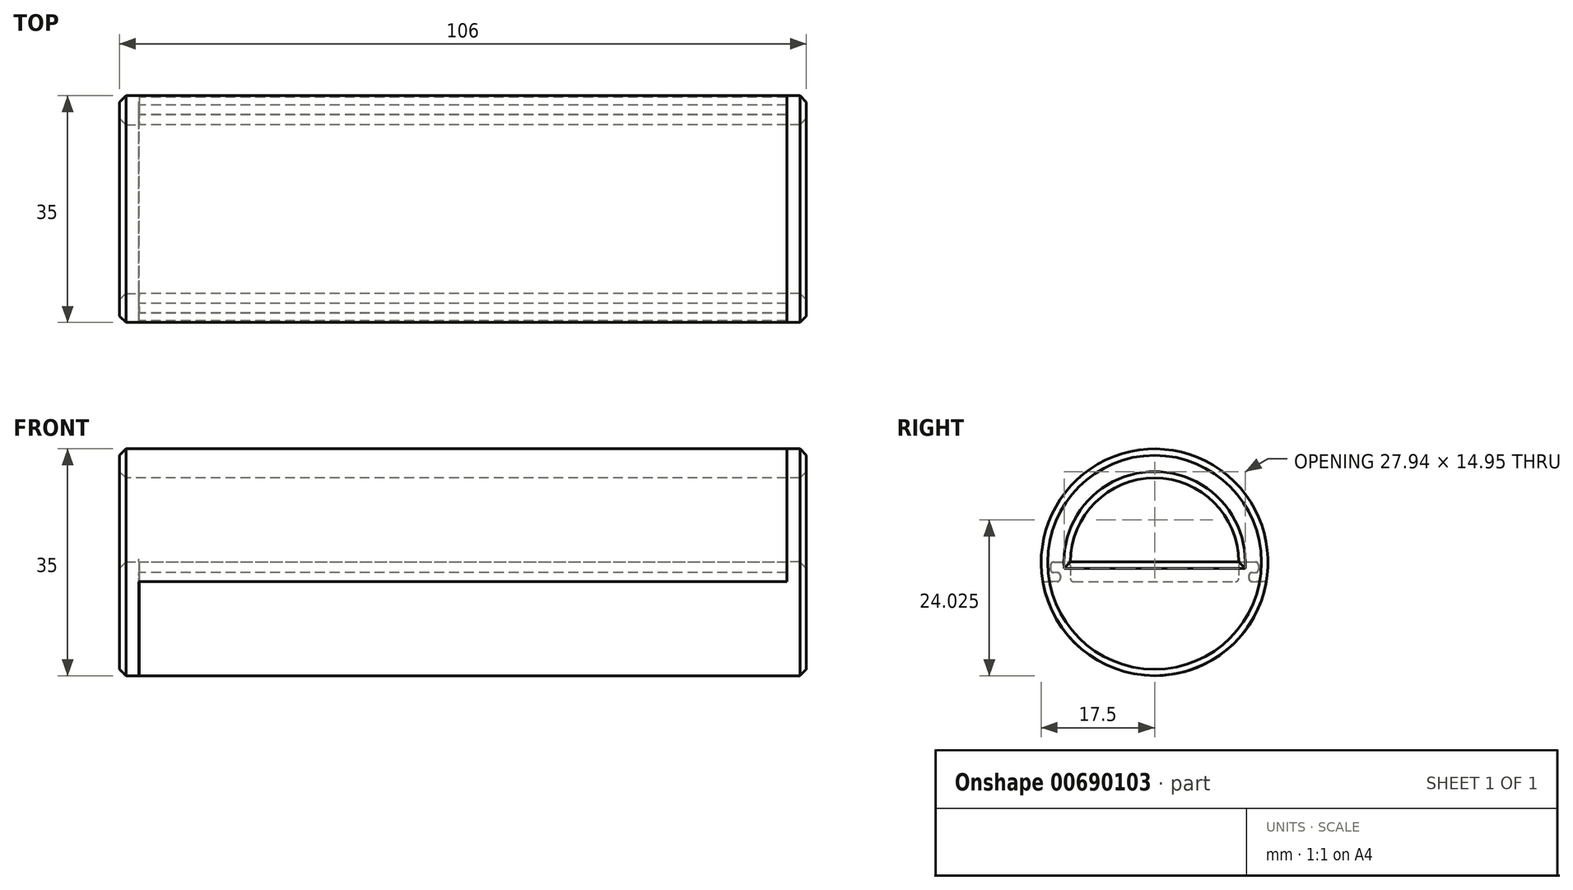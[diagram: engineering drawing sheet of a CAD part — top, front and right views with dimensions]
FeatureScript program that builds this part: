
annotation { "Feature Type Name" : "Feature", "Feature Type Description" : "" }
export const myFeature = defineFeature(function(context is Context, id is Id, definition is map)
    precondition{}
    {
        {
            var Q0;
            Q0=qCreatedBy(makeId("Right.planeOp"),FACE);
            var sketch = newSketch(context, id + "F0", { "sketchPlane" : qUnion([Q0])});
            skCircle(sketch, "E0", {"center": v(0, 0) * mm, "radius": 17.5 * mm});
            skLineSegment(sketch, "E1.top", {"start": v(-17.24, -3) * mm, "end": v(-14.53, -3) * mm});
            skLineSegment(sketch, "E1.right", {"start": v(-14.53, -1.56) * mm, "end": v(-14.53, -3) * mm});
            skLineSegment(sketch, "E2.top", {"start": v(-14.53, -1.56) * mm, "end": v(-16.03, -1.56) * mm});
            skLineSegment(sketch, "E2.right", {"start": v(-16.03, 0) * mm, "end": v(-16.03, -1.56) * mm});
            skLineSegment(sketch, "E3", {"start": v(-13, 0) * mm, "end": v(-13, -3) * mm});
            skPoint(sketch, "E4.orphan", {"position": v(-17.5, 0) * mm});
            skLineSegment(sketch, "E5", {"start": v(-16.03, 0) * mm, "end": v(-13, 0) * mm});
            skLineSegment(sketch, "E6.3", {"start": v(-14.58, -1.6) * mm, "end": v(-14.58, -2.95) * mm});
            skLineSegment(sketch, "E6.4", {"start": v(-14.58, -1.6) * mm, "end": v(-16.08, -1.6) * mm});
            skLineSegment(sketch, "E6.5", {"start": v(-16.08, 0.05) * mm, "end": v(-16.08, -1.6) * mm});
            skLineSegment(sketch, "E7", {"start": v(-14.58, -2.95) * mm, "end": v(-17.25, -2.95) * mm});
            skLineSegment(sketch, "E8.MirrorCS", {"start": v(14.58, -2.95) * mm, "end": v(17.25, -2.95) * mm});
            skLineSegment(sketch, "E9.MirrorCS", {"start": v(16.03, 0) * mm, "end": v(16.03, -1.56) * mm});
            skLineSegment(sketch, "E10.MirrorCS", {"start": v(14.53, -1.56) * mm, "end": v(16.03, -1.56) * mm});
            skLineSegment(sketch, "E11.MirrorCS", {"start": v(16.03, 0) * mm, "end": v(13, 0) * mm});
            skLineSegment(sketch, "E12.MirrorCS", {"start": v(14.53, -1.56) * mm, "end": v(14.53, -3) * mm});
            skLineSegment(sketch, "E13.MirrorCS", {"start": v(14.58, -1.6) * mm, "end": v(14.58, -2.95) * mm});
            skLineSegment(sketch, "E14.MirrorCS", {"start": v(16.08, 0.05) * mm, "end": v(16.08, -1.6) * mm});
            skLineSegment(sketch, "E15.MirrorCS", {"start": v(17.24, -3) * mm, "end": v(14.53, -3) * mm});
            skLineSegment(sketch, "E16.MirrorCS", {"start": v(13, 0) * mm, "end": v(13, -3) * mm});
            skPoint(sketch, "E17.MirrorP", {"position": v(17.5, 0) * mm});
            skLineSegment(sketch, "E18.MirrorCS", {"start": v(14.58, -1.6) * mm, "end": v(16.08, -1.6) * mm});
            skLineSegment(sketch, "E19", {"start": v(-13, -3) * mm, "end": v(13, -3) * mm});
            skLineSegment(sketch, "E20", {"start": v(-16.08, 0.05) * mm, "end": v(16.08, 0.05) * mm});
            skArc(sketch, "E21", {"start": v(13, 0) * mm, "mid": v(0, 13) * mm, "end": v(-13, 0) * mm});
            skSolve(sketch);
        }
        {
            var Q0;
            Q0=makeQuery(id+"F0.imprint","IMPRINT",FACE,{"disambiguationData":[TD([[makeQuery(id+"F0.imprint","IMPRINT",EDGE,{"derivedFrom":sQuery(id+"F0.wireOp",EDGE,"E6.3")}),-1.0]])]});
            extrude(context, id + "F1", {"entities" : qUnion([Q0]), "depth" : 99.97 * mm, "offsetDistance" : 25 * mm});
        }
        {
            var Q0;
            Q0 = qSketchRegion(id + "F0", true);
            var Q1;
            {var subQ0=sQuery(id+"F0.wireOp",EDGE,"E21");var subQ1=sQuery(id+"F0.wireOp",EDGE,"E20");var subQ2=makeQuery(id+"F0.imprint","INTERSECT",VERTEX,{"disambiguationData":[OD(0.0)],"derivedFrom":[subQ1,subQ0]});Q1=makeQuery(id+"F0.imprint","IMPRINT",FACE,{"disambiguationData":[TD([[makeQuery(id+"F0.imprint","IMPRINT",EDGE,{"disambiguationData":[TD([[subQ2,-1.0]])],"derivedFrom":subQ1}),1.0]])]});}
            var Q2;
            {var subQ5=sQuery(id+"F0.wireOp",EDGE,"E3");Q2=makeQuery(id+"F0.imprint","IMPRINT",FACE,{"disambiguationData":[TD([[makeQuery(id+"F0.imprint","IMPRINT",EDGE,{"derivedFrom":subQ5}),1.0]])]});}
            extrude(context, id + "F2", {"entities" : qUnion([Q0, Q1, Q2]), "operationType" : NewBodyOperationType.ADD, "oppositeDirection" : true, "depth" : 3 * mm, "offsetDistance" : 25 * mm});
        }
        {
            var Q0;
            {var subQ0=sQuery(id+"F0.wireOp",EDGE,"E1.top");Q0=makeQuery(id+"F0.imprint","IMPRINT",FACE,{"disambiguationData":[TD([[makeQuery(id+"F0.imprint","IMPRINT",EDGE,{"derivedFrom":subQ0}),-1.0]])]});}
            extrude(context, id + "F3", {"entities" : qUnion([Q0]), "depth" : 100 * mm, "offsetDistance" : 25 * mm, "hasSecondDirection" : true, "secondDirectionOppositeDirection" : false, "secondDirectionDepth" : 0.03 * mm});
        }
        {
            var Q0;
            Q0 = qSketchRegion(id + "F0", true);
            var Q1;
            {var subQ0=sQuery(id+"F0.wireOp",EDGE,"E21");var subQ1=sQuery(id+"F0.wireOp",EDGE,"E20");var subQ2=makeQuery(id+"F0.imprint","INTERSECT",VERTEX,{"disambiguationData":[OD(0.0)],"derivedFrom":[subQ1,subQ0]});Q1=makeQuery(id+"F0.imprint","IMPRINT",FACE,{"disambiguationData":[TD([[makeQuery(id+"F0.imprint","IMPRINT",EDGE,{"disambiguationData":[TD([[subQ2,-1.0]])],"derivedFrom":subQ1}),1.0]])]});}
            var Q2;
            {var subQ5=sQuery(id+"F0.wireOp",EDGE,"E3");Q2=makeQuery(id+"F0.imprint","IMPRINT",FACE,{"disambiguationData":[TD([[makeQuery(id+"F0.imprint","IMPRINT",EDGE,{"derivedFrom":subQ5}),1.0]])]});}
            extrude(context, id + "F4", {"entities" : qUnion([Q0, Q1, Q2]), "operationType" : NewBodyOperationType.ADD, "depth" : 103 * mm, "offsetDistance" : 25 * mm, "hasSecondDirection" : true, "secondDirectionOppositeDirection" : false, "secondDirectionDepth" : 100 * mm});
        }
        {
            var Q0;
            Q0=makeQuery(id+"F2.opExtrude","CAP_FACE",FACE,{"disambiguationData":[OSD([sQuery(id+"F0.wireOp",EDGE,"E0")])],"isStart":false});
            var Q1;
            Q1=makeQuery(id+"F4.opExtrude","CAP_FACE",FACE,{"disambiguationData":[OSD([sQuery(id+"F0.wireOp",EDGE,"E0")])],"isStart":false});
            chamfer(context, id + "F5", {"entities" : qUnion([Q0, Q1]), "width" : 1 * mm, "tangentPropagation" : true});
        }
        {
            var Q0;
            Q0=makeQuery(id+"F3.opExtrude","SWEPT_EDGE",EDGE,{"disambiguationData":[OSD([sQuery(id+"F0.wireOp",EDGE,"E11.MirrorCS"),sQuery(id+"F0.wireOp",EDGE,"E16.MirrorCS")])]});
            var Q1;
            Q1=makeQuery(id+"F1.opExtrude","SWEPT_EDGE",EDGE,{"disambiguationData":[OSD([sQuery(id+"F0.wireOp",EDGE,"E14.MirrorCS"),sQuery(id+"F0.wireOp",EDGE,"E20")])]});
            var Q2;
            Q2=makeQuery(id+"F3.opExtrude","SWEPT_EDGE",EDGE,{"disambiguationData":[OSD([sQuery(id+"F0.wireOp",EDGE,"E9.MirrorCS"),sQuery(id+"F0.wireOp",EDGE,"E11.MirrorCS")])]});
            var Q3;
            Q3=makeQuery(id+"F1.opExtrude","SWEPT_EDGE",EDGE,{"disambiguationData":[OSD([sQuery(id+"F0.wireOp",EDGE,"E14.MirrorCS"),sQuery(id+"F0.wireOp",EDGE,"E18.MirrorCS")])]});
            var Q4;
            Q4=makeQuery(id+"F3.opExtrude","SWEPT_EDGE",EDGE,{"disambiguationData":[OSD([sQuery(id+"F0.wireOp",EDGE,"E9.MirrorCS"),sQuery(id+"F0.wireOp",EDGE,"E10.MirrorCS")])]});
            var Q5;
            Q5=makeQuery(id+"F3.opExtrude","SWEPT_EDGE",EDGE,{"disambiguationData":[OSD([sQuery(id+"F0.wireOp",EDGE,"E10.MirrorCS"),sQuery(id+"F0.wireOp",EDGE,"E12.MirrorCS")])]});
            var Q6;
            Q6=makeQuery(id+"F1.opExtrude","SWEPT_EDGE",EDGE,{"disambiguationData":[OSD([sQuery(id+"F0.wireOp",EDGE,"E13.MirrorCS"),sQuery(id+"F0.wireOp",EDGE,"E18.MirrorCS")])]});
            var Q7;
            Q7=makeQuery(id+"F3.opExtrude","SWEPT_EDGE",EDGE,{"disambiguationData":[OSD([sQuery(id+"F0.wireOp",EDGE,"E16.MirrorCS"),sQuery(id+"F0.wireOp",EDGE,"E19")])]});
            var Q8;
            Q8=makeQuery(id+"F1.opExtrude","SWEPT_EDGE",EDGE,{"disambiguationData":[OSD([sQuery(id+"F0.wireOp",EDGE,"E8.MirrorCS"),sQuery(id+"F0.wireOp",EDGE,"E13.MirrorCS")])]});
            var Q9;
            Q9=makeQuery(id+"F3.opExtrude","SWEPT_EDGE",EDGE,{"disambiguationData":[OSD([sQuery(id+"F0.wireOp",EDGE,"E12.MirrorCS"),sQuery(id+"F0.wireOp",EDGE,"E15.MirrorCS")])]});
            var Q10;
            Q10=makeQuery(id+"F3.opExtrude","SWEPT_EDGE",EDGE,{"disambiguationData":[OSD([sQuery(id+"F0.wireOp",EDGE,"E3"),sQuery(id+"F0.wireOp",EDGE,"E5")])]});
            var Q11;
            Q11=makeQuery(id+"F3.opExtrude","SWEPT_EDGE",EDGE,{"disambiguationData":[OSD([sQuery(id+"F0.wireOp",EDGE,"E3"),sQuery(id+"F0.wireOp",EDGE,"E19")])]});
            var Q12;
            Q12=makeQuery(id+"F3.opExtrude","SWEPT_EDGE",EDGE,{"disambiguationData":[OSD([sQuery(id+"F0.wireOp",EDGE,"E1.right"),sQuery(id+"F0.wireOp",EDGE,"E2.top")])]});
            var Q13;
            Q13=makeQuery(id+"F1.opExtrude","SWEPT_EDGE",EDGE,{"disambiguationData":[OSD([sQuery(id+"F0.wireOp",EDGE,"E6.3"),sQuery(id+"F0.wireOp",EDGE,"E6.4")])]});
            var Q14;
            Q14=makeQuery(id+"F3.opExtrude","SWEPT_EDGE",EDGE,{"disambiguationData":[OSD([sQuery(id+"F0.wireOp",EDGE,"E1.top"),sQuery(id+"F0.wireOp",EDGE,"E1.right")])]});
            var Q15;
            Q15=makeQuery(id+"F1.opExtrude","SWEPT_EDGE",EDGE,{"disambiguationData":[OSD([sQuery(id+"F0.wireOp",EDGE,"E6.3"),sQuery(id+"F0.wireOp",EDGE,"E7")])]});
            var Q16;
            Q16=makeQuery(id+"F3.opExtrude","SWEPT_EDGE",EDGE,{"disambiguationData":[OSD([sQuery(id+"F0.wireOp",EDGE,"E2.top"),sQuery(id+"F0.wireOp",EDGE,"E2.right")])]});
            var Q17;
            Q17=makeQuery(id+"F1.opExtrude","SWEPT_EDGE",EDGE,{"disambiguationData":[OSD([sQuery(id+"F0.wireOp",EDGE,"E6.4"),sQuery(id+"F0.wireOp",EDGE,"E6.5")])]});
            var Q18;
            Q18=makeQuery(id+"F1.opExtrude","SWEPT_EDGE",EDGE,{"disambiguationData":[OSD([sQuery(id+"F0.wireOp",EDGE,"E6.5"),sQuery(id+"F0.wireOp",EDGE,"E20")])]});
            var Q19;
            Q19=makeQuery(id+"F3.opExtrude","SWEPT_EDGE",EDGE,{"disambiguationData":[OSD([sQuery(id+"F0.wireOp",EDGE,"E2.right"),sQuery(id+"F0.wireOp",EDGE,"E5")])]});
            var Q20;
            {var subQ0=sQuery(id+"F0.wireOp",EDGE,"E21");var subQ1=sQuery(id+"F0.wireOp",EDGE,"E20");Q20=makeQuery(id+"F1.opExtrude","SWEPT_EDGE",EDGE,{"disambiguationData":[OSD([subQ1,subQ0]),TDD([makeQuery(id+"F0.imprint","INTERSECT",VERTEX,{"disambiguationData":[OD(0.0)],"derivedFrom":[subQ1,subQ0]})])]});}
            var Q21;
            {var subQ0=sQuery(id+"F0.wireOp",EDGE,"E21");var subQ1=sQuery(id+"F0.wireOp",EDGE,"E20");Q21=makeQuery(id+"F1.opExtrude","SWEPT_EDGE",EDGE,{"disambiguationData":[OSD([subQ1,subQ0]),TDD([makeQuery(id+"F0.imprint","INTERSECT",VERTEX,{"disambiguationData":[OD(1.0)],"derivedFrom":[subQ1,subQ0]})])]});}
            fillet(context, id + "F6", {"entities" : qUnion([Q0, Q1, Q2, Q3, Q4, Q5, Q6, Q7, Q8, Q9, Q10, Q11, Q12, Q13, Q14, Q15, Q16, Q17, Q18, Q19, Q20, Q21]), "radius" : .5 * mm, "tangentPropagation" : true, "allowEdgeOverflow" : false});
        }
    });
